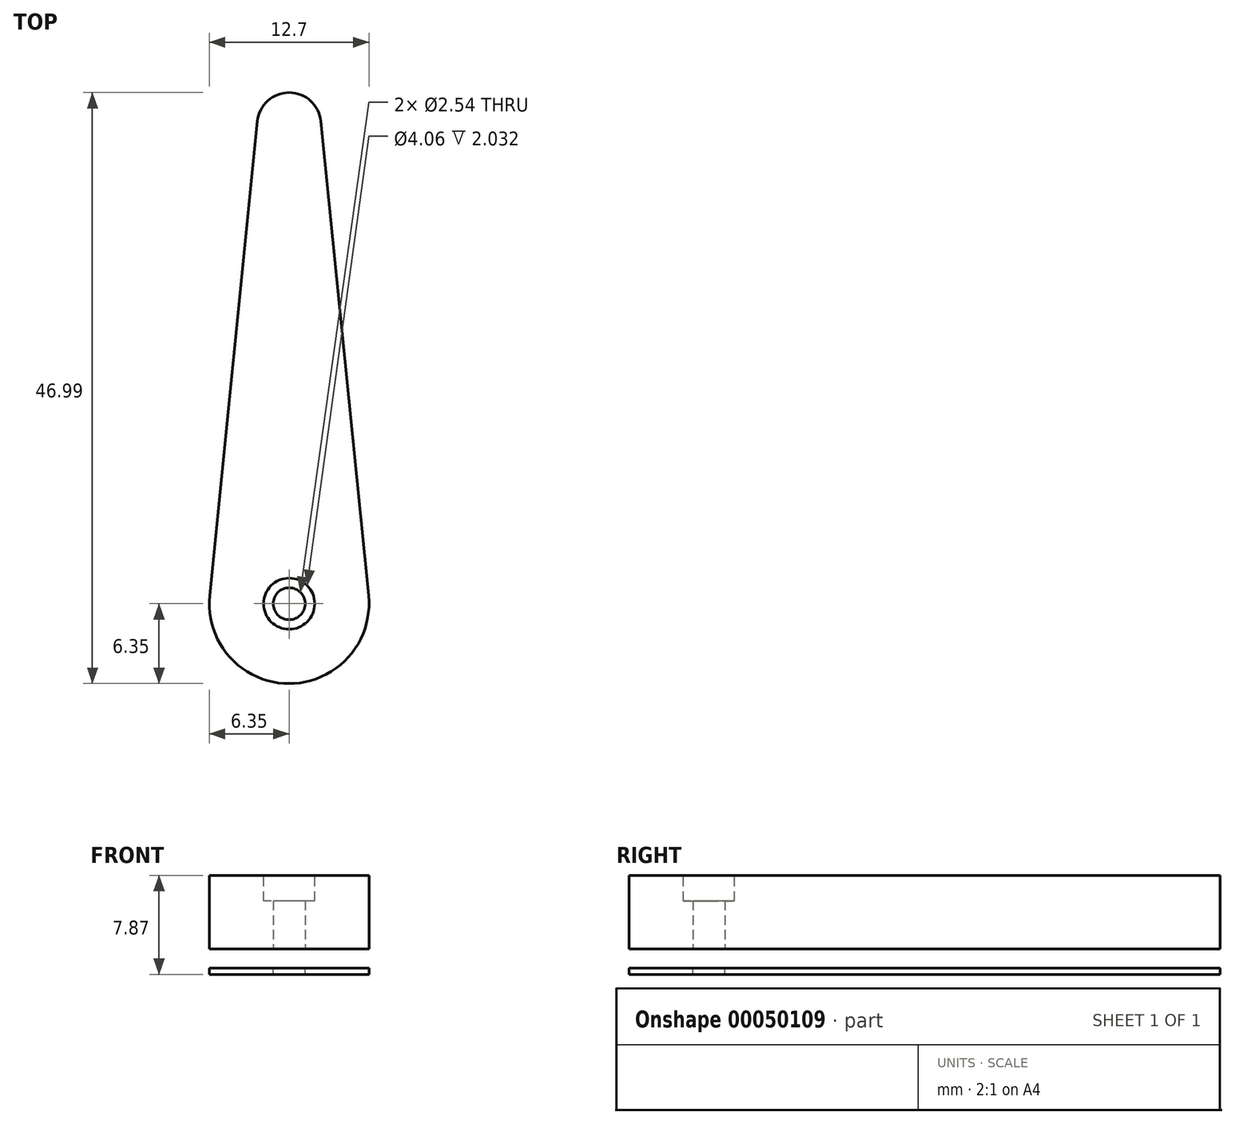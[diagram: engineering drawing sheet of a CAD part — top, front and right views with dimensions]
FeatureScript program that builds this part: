
annotation { "Feature Type Name" : "Feature", "Feature Type Description" : "" }
export const myFeature = defineFeature(function(context is Context, id is Id, definition is map)
    precondition{}
    {
        {
            var Q0;
            Q0=qCreatedBy(makeId("Top.planeOp"),FACE);
            var sketch = newSketch(context, id + "F0", { "sketchPlane" : qUnion([Q0])});
            skCircle(sketch, "E0", {"center": v(0, 0) * mm, "radius": 1.27 * mm});
            skArc(sketch, "E1", {"start": v(-6.32, 0.63) * mm, "mid": v(0, -6.35) * mm, "end": v(6.32, 0.63) * mm});
            skLineSegment(sketch, "E2", {"start": v(6.32, 0.63) * mm, "end": v(2.53, 38.35) * mm});
            skLineSegment(sketch, "E3", {"start": v(-2.53, 38.35) * mm, "end": v(-6.32, 0.64) * mm});
            skPoint(sketch, "E4.visualSharp", {"position": v(0, 63.5) * mm});
            skArc(sketch, "E4.filletArc", {"start": v(2.53, 38.35) * mm, "mid": v(0, 40.64) * mm, "end": v(-2.53, 38.35) * mm});
            skSolve(sketch);
        }
        {
            var Q0;
            Q0 = qSketchRegion(id + "F0", true);
            extrude(context, id + "F1", {"entities" : qUnion([Q0]), "depth" : 5.84 * mm});
        }
        {
            var Q0;
            Q0=makeQuery(id+"F1.opExtrude","CAP_FACE",FACE,{"disambiguationData":[OSD([sQuery(id+"F0.wireOp",EDGE,"E0"),sQuery(id+"F0.wireOp",EDGE,"E1"),sQuery(id+"F0.wireOp",EDGE,"E2"),sQuery(id+"F0.wireOp",EDGE,"E3"),sQuery(id+"F0.wireOp",EDGE,"E4.filletArc")])],"isStart":false});
            var sketch = newSketch(context, id + "F2", { "sketchPlane" : qUnion([Q0])});
            skCircle(sketch, "E5", {"center": v(0, 0) * mm, "radius": 2.03 * mm});
            skSolve(sketch);
        }
        {
            var Q0;
            Q0 = qSketchRegion(id + "F2", true);
            extrude(context, id + "F3", {"entities" : qUnion([Q0]), "operationType" : NewBodyOperationType.REMOVE, "oppositeDirection" : true, "depth" : 2.03 * mm});
        }
        {
            var Q0;
            Q0=makeQuery(id+"F1.opExtrude","CAP_FACE",FACE,{"disambiguationData":[OSD([sQuery(id+"F0.wireOp",EDGE,"E0"),sQuery(id+"F0.wireOp",EDGE,"E1"),sQuery(id+"F0.wireOp",EDGE,"E2"),sQuery(id+"F0.wireOp",EDGE,"E3"),sQuery(id+"F0.wireOp",EDGE,"E4.filletArc")])],"isStart":true});
            cPlane(context, id + "F4", {"entities" : qUnion([Q0]), "cplaneType" : CPlaneType.OFFSET, "offset" : 1.52 * mm, "width" : 152.4 * mm, "height" : 152.4 * mm});
        }
        {
            var Q0;
            Q0=qCreatedBy(id+"F4.planeOp",FACE);
            var sketch = newSketch(context, id + "F5", { "sketchPlane" : qUnion([Q0])});
            skLineSegment(sketch, "E6.0.0", {"start": v(-6.32, -0.64) * mm, "end": v(-2.53, -38.35) * mm});
            skArc(sketch, "E6.0.1", {"start": v(-2.53, -38.35) * mm, "mid": v(0, -40.64) * mm, "end": v(2.53, -38.35) * mm});
            skLineSegment(sketch, "E6.0.2", {"start": v(2.53, -38.35) * mm, "end": v(6.32, -0.63) * mm});
            skArc(sketch, "E6.0.3", {"start": v(6.32, -0.63) * mm, "mid": v(0, 6.35) * mm, "end": v(-6.32, -0.63) * mm});
            skCircle(sketch, "E7.0", {"center": v(0, 0) * mm, "radius": 1.27 * mm});
            skSolve(sketch);
        }
        {
            var Q0;
            Q0 = qSketchRegion(id + "F5", true);
            extrude(context, id + "F6", {"entities" : qUnion([Q0]), "operationType" : NewBodyOperationType.ADD, "depth" : 0.5 * mm});
        }
    });
